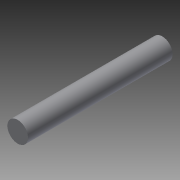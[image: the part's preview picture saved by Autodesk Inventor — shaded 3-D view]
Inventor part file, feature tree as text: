
AUTODESK INVENTOR PART (.ipt)
format: ipt  version: 2013 (Build 170138000, 138)  size: 67,072 bytes
history: native  units: in
note: dims shown in document units (in); Inventor stores cm internally (conversion verified against a paired STEP export)
features: extrude x1, sketch x1
ambient origin geometry x8: Origin, YZ Plane, XZ Plane, XY Plane, X Axis, Y Axis, Z Axis, Center Point
bodies: Solid1 (feature_tree)
feature tree (2):
  extrude  "Extrusion1"  Depth=14.0in TaperAngle=0.0deg
  sketch  "Sketch1"  dims[d0=2.0in d1=14.0in d2=0.0in]
